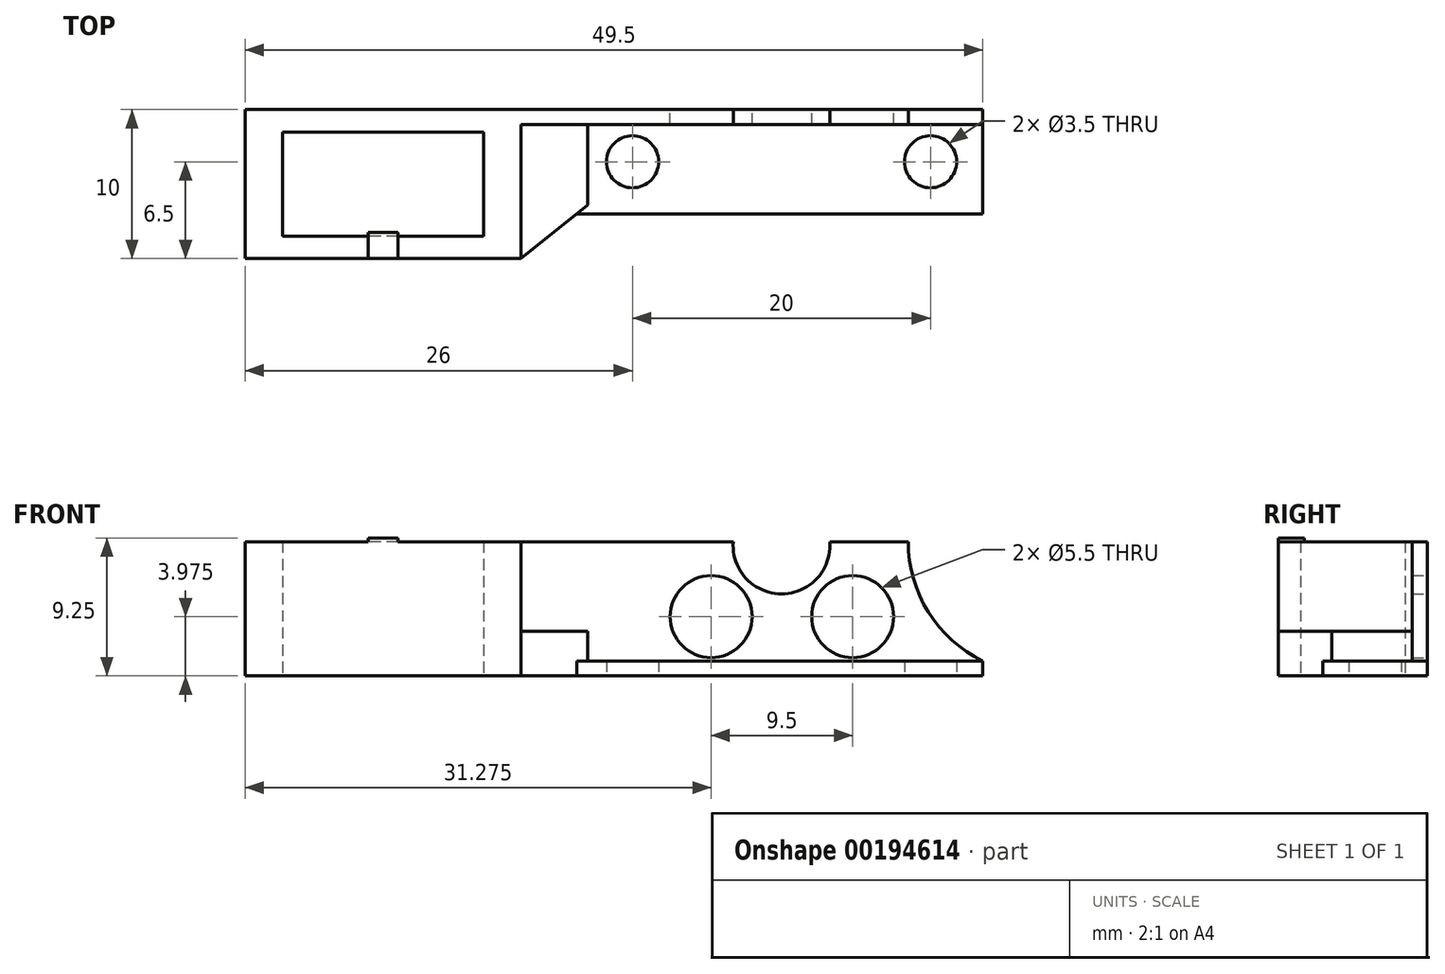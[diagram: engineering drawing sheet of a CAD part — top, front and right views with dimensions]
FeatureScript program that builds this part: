
annotation { "Feature Type Name" : "Feature", "Feature Type Description" : "" }
export const myFeature = defineFeature(function(context is Context, id is Id, definition is map)
    precondition{}
    {
        {
            var Q0;
            Q0=qCreatedBy(makeId("Top.planeOp"),FACE);
            var sketch = newSketch(context, id + "F0", { "sketchPlane" : qUnion([Q0])});
            skLineSegment(sketch, "E0.bottom", {"start": v(6.75, 3.5) * mm, "end": v(-6.75, 3.5) * mm});
            skLineSegment(sketch, "E0.top", {"start": v(6.75, -3.5) * mm, "end": v(-6.75, -3.5) * mm});
            skLineSegment(sketch, "E0.left", {"start": v(6.75, 3.5) * mm, "end": v(6.75, -3.5) * mm});
            skLineSegment(sketch, "E0.right", {"start": v(-6.75, 3.5) * mm, "end": v(-6.75, -3.5) * mm});
            skPoint(sketch, "E0.middle", {"position": v(0, 0) * mm});
            skLineSegment(sketch, "E1.bottom", {"start": v(-9.25, 5) * mm, "end": v(9.25, 5) * mm});
            skLineSegment(sketch, "E1.top", {"start": v(-9.25, -5) * mm, "end": v(9.25, -5) * mm});
            skLineSegment(sketch, "E1.left", {"start": v(-9.25, 5) * mm, "end": v(-9.25, -5) * mm});
            skLineSegment(sketch, "E1.right", {"start": v(9.25, 5) * mm, "end": v(9.25, -5) * mm});
            skSolve(sketch);
        }
        {
            var Q0;
            Q0=makeQuery(id+"F0.imprint","IMPRINT",FACE,{"disambiguationData":[TD([[makeQuery(id+"F0.imprint","IMPRINT",EDGE,{"derivedFrom":sQuery(id+"F0.wireOp",EDGE,"E0.bottom")}),-1.0]])]});
            extrude(context, id + "F1", {"entities" : qUnion([Q0]), "depth" : 9 * mm});
        }
        {
            var Q0;
            Q0=makeQuery(id+"F1.opExtrude","CAP_FACE",FACE,{"disambiguationData":[OSD([sQuery(id+"F0.wireOp",EDGE,"E0.bottom"),sQuery(id+"F0.wireOp",EDGE,"E0.top"),sQuery(id+"F0.wireOp",EDGE,"E0.left"),sQuery(id+"F0.wireOp",EDGE,"E0.right"),sQuery(id+"F0.wireOp",EDGE,"E1.bottom"),sQuery(id+"F0.wireOp",EDGE,"E1.top"),sQuery(id+"F0.wireOp",EDGE,"E1.left"),sQuery(id+"F0.wireOp",EDGE,"E1.right")])],"isStart":true});
            var sketch = newSketch(context, id + "F2", { "sketchPlane" : qUnion([Q0])});
            skLineSegment(sketch, "E2.bottom", {"start": v(14.25, -5) * mm, "end": v(39.25, -5) * mm});
            skLineSegment(sketch, "E2.top", {"start": v(14.25, 1) * mm, "end": v(39.25, 1) * mm});
            skLineSegment(sketch, "E2.left", {"start": v(14.25, -5) * mm, "end": v(14.25, 1) * mm});
            skLineSegment(sketch, "E2.right", {"start": v(39.25, -5) * mm, "end": v(39.25, 1) * mm});
            skLineSegment(sketch, "E3", {"start": v(14.25, -4) * mm, "end": v(39.25, -4) * mm});
            skLineSegment(sketch, "E4", {"start": v(19.25, 1) * mm, "end": v(19.25, -4) * mm, "construction": true});
            skLineSegment(sketch, "E5", {"start": v(34.25, 1) * mm, "end": v(34.25, -4) * mm, "construction": true});
            skLineSegment(sketch, "E6", {"start": v(34.25, -4) * mm, "end": v(39.25, 1) * mm, "construction": true});
            skLineSegment(sketch, "E7", {"start": v(14.25, 1) * mm, "end": v(19.25, -4) * mm, "construction": true});
            skLineSegment(sketch, "E8", {"start": v(14.25, -5) * mm, "end": v(9.25, -5) * mm});
            skLineSegment(sketch, "E9", {"start": v(9.25, -5) * mm, "end": v(9.25, 5) * mm});
            skLineSegment(sketch, "E10", {"start": v(9.25, 5) * mm, "end": v(14.25, 1) * mm});
            skCircle(sketch, "E11", {"center": v(16.75, -1.5) * mm, "radius": 1.75 * mm});
            skCircle(sketch, "E12", {"center": v(36.75, -1.5) * mm, "radius": 1.75 * mm});
            skLineSegment(sketch, "E13", {"start": v(39.25, -5) * mm, "end": v(40.25, -5) * mm});
            skLineSegment(sketch, "E14", {"start": v(40.25, -5) * mm, "end": v(40.25, 2) * mm});
            skLineSegment(sketch, "E15", {"start": v(40.25, 2) * mm, "end": v(13, 2) * mm});
            skLineSegment(sketch, "E16", {"start": v(13.75, -5) * mm, "end": v(13.75, 1.4) * mm});
            skSolve(sketch);
        }
        {
            var Q0;
            {var subQ3=sQuery(id+"F2.wireOp",EDGE,"E9");Q0=makeQuery(id+"F2.imprint","IMPRINT",FACE,{"disambiguationData":[TD([[makeQuery(id+"F2.imprint","IMPRINT",EDGE,{"derivedFrom":subQ3}),-1.0]])]});}
            extrude(context, id + "F3", {"entities" : qUnion([Q0]), "operationType" : NewBodyOperationType.ADD, "oppositeDirection" : true, "depth" : 3 * mm});
        }
        {
            var Q0;
            {var subQ3=sQuery(id+"F2.wireOp",EDGE,"E16");Q0=makeQuery(id+"F2.imprint","IMPRINT",FACE,{"disambiguationData":[TD([[makeQuery(id+"F2.imprint","IMPRINT",EDGE,{"derivedFrom":subQ3}),-1.0]])]});}
            var Q1;
            {var subQ1=sQuery(id+"F2.wireOp",EDGE,"E2.top");Q1=makeQuery(id+"F2.imprint","IMPRINT",FACE,{"disambiguationData":[TD([[makeQuery(id+"F2.imprint","IMPRINT",EDGE,{"derivedFrom":subQ1}),1.0]])]});}
            var Q2;
            {var subQ0=sQuery(id+"F2.wireOp",EDGE,"E2.bottom");Q2=makeQuery(id+"F2.imprint","IMPRINT",FACE,{"disambiguationData":[TD([[makeQuery(id+"F2.imprint","IMPRINT",EDGE,{"derivedFrom":subQ0}),1.0]])]});}
            var Q3;
            {var subQ2=sQuery(id+"F2.wireOp",EDGE,"E2.top");Q3=makeQuery(id+"F2.imprint","IMPRINT",FACE,{"disambiguationData":[TD([[makeQuery(id+"F2.imprint","IMPRINT",EDGE,{"derivedFrom":subQ2}),-1.0]])]});}
            extrude(context, id + "F4", {"entities" : qUnion([Q0, Q1, Q2, Q3]), "operationType" : NewBodyOperationType.ADD, "oppositeDirection" : true, "depth" : 1 * mm});
        }
        {
            var Q0;
            {var subQ0=sQuery(id+"F2.wireOp",EDGE,"E8");Q0=makeQuery(id+"F4.boolean.opBoolean","MERGE",FACE,{"derivedFrom":[makeQuery(id+"F3.boolean.opBoolean","MERGE",FACE,{"derivedFrom":[makeQuery(id+"F1.opExtrude","SWEPT_FACE",FACE,{"disambiguationData":[OSD([sQuery(id+"F0.wireOp",EDGE,"E1.bottom")])]}),makeQuery(id+"F3.opExtrude","SWEPT_FACE",FACE,{"disambiguationData":[OSD([subQ0])]})]}),makeQuery(id+"F4.opExtrude","SWEPT_FACE",FACE,{"disambiguationData":[OSD([sQuery(id+"F2.wireOp",EDGE,"E2.bottom"),subQ0,sQuery(id+"F2.wireOp",EDGE,"E13")])]})]});}
            var sketch = newSketch(context, id + "F5", { "sketchPlane" : qUnion([Q0])});
            skLineSegment(sketch, "E17.bottom", {"start": v(-14.25, 1) * mm, "end": v(-39.25, 1) * mm});
            skLineSegment(sketch, "E17.top", {"start": v(-14.25, 16.5) * mm, "end": v(-39.25, 16.5) * mm});
            skLineSegment(sketch, "E17.left", {"start": v(-14.25, 1) * mm, "end": v(-14.25, 16.5) * mm});
            skLineSegment(sketch, "E17.right", {"start": v(-39.25, 1) * mm, "end": v(-39.25, 16.5) * mm});
            skLineSegment(sketch, "E18", {"start": v(-26.75, 16.5) * mm, "end": v(-26.75, 1) * mm, "construction": true});
            skLineSegment(sketch, "E19", {"start": v(-39.25, 8.75) * mm, "end": v(-14.25, 8.75) * mm, "construction": true});
            skCircle(sketch, "E20", {"center": v(-26.75, 8.75) * mm, "radius": 3.25 * mm});
            skLineSegment(sketch, "E21", {"start": v(-22.02, 16.5) * mm, "end": v(-22.02, 1) * mm, "construction": true});
            skLineSegment(sketch, "E22", {"start": v(-31.52, 16.5) * mm, "end": v(-31.52, 1) * mm, "construction": true});
            skLineSegment(sketch, "E23", {"start": v(-31.52, 3.97) * mm, "end": v(-22.02, 3.98) * mm, "construction": true});
            skLineSegment(sketch, "E24", {"start": v(-31.52, 13.47) * mm, "end": v(-22.02, 13.48) * mm, "construction": true});
            skCircle(sketch, "E25", {"center": v(-22.02, 13.48) * mm, "radius": 2.75 * mm});
            skCircle(sketch, "E26", {"center": v(-22.02, 3.98) * mm, "radius": 2.75 * mm});
            skCircle(sketch, "E27", {"center": v(-31.52, 3.97) * mm, "radius": 2.75 * mm});
            skCircle(sketch, "E28", {"center": v(-31.52, 13.47) * mm, "radius": 2.75 * mm});
            skLineSegment(sketch, "E29.bottom", {"start": v(-14.25, 16.5) * mm, "end": v(-9.25, 16.5) * mm});
            skLineSegment(sketch, "E29.top", {"start": v(-14.25, 1) * mm, "end": v(-9.25, 1) * mm});
            skLineSegment(sketch, "E29.left", {"start": v(-14.25, 16.5) * mm, "end": v(-14.25, 1) * mm});
            skLineSegment(sketch, "E29.right", {"start": v(-9.25, 16.5) * mm, "end": v(-9.25, 1) * mm});
            skLineSegment(sketch, "E30.bottom", {"start": v(-39.25, 16.5) * mm, "end": v(-40.25, 16.5) * mm});
            skLineSegment(sketch, "E30.top", {"start": v(-39.25, 1) * mm, "end": v(-40.25, 1) * mm});
            skLineSegment(sketch, "E30.left", {"start": v(-39.25, 16.5) * mm, "end": v(-39.25, 1) * mm});
            skLineSegment(sketch, "E30.right", {"start": v(-40.25, 16.5) * mm, "end": v(-40.25, 1) * mm});
            skLineSegment(sketch, "E31", {"start": v(-9.25, 9) * mm, "end": v(-40.25, 9) * mm});
            skArc(sketch, "E32", {"start": v(-40.25, 1) * mm, "mid": v(-36.6, 4.28) * mm, "end": v(-35.25, 9) * mm});
            skSolve(sketch);
        }
        {
            var Q0;
            {var subQ1=sQuery(id+"F5.wireOp",EDGE,"E17.bottom");Q0=makeQuery(id+"F5.imprint","IMPRINT",FACE,{"disambiguationData":[TD([[makeQuery(id+"F5.imprint","IMPRINT",EDGE,{"derivedFrom":subQ1}),1.0]])]});}
            var Q1;
            {var subQ5=sQuery(id+"F2.wireOp",EDGE,"E8");var subQ6=makeQuery(id+"F3.opExtrude","CAP_EDGE",EDGE,{"disambiguationData":[OSD([subQ5])],"isStart":false});Q1=makeQuery(id+"F5.imprint","IMPRINT",FACE,{"disambiguationData":[TD([[makeQuery(id+"F5.imprint","IMPRINT",EDGE,{"derivedFrom":subQ6}),1.0]])]});}
            var Q2;
            {var subQ0=sQuery(id+"F5.wireOp",EDGE,"E30.top");Q2=makeQuery(id+"F5.imprint","IMPRINT",FACE,{"disambiguationData":[TD([[makeQuery(id+"F5.imprint","IMPRINT",EDGE,{"derivedFrom":subQ0}),1.0]])]});}
            extrude(context, id + "F6", {"entities" : qUnion([Q0, Q1, Q2]), "operationType" : NewBodyOperationType.ADD, "oppositeDirection" : true, "depth" : 1 * mm});
        }
        {
            var Q0;
            {var subQ0=sQuery(id+"F5.wireOp",EDGE,"E31");var subQ1=makeQuery(id+"F5.imprint","INTERSECT",VERTEX,{"derivedFrom":[sQuery(id+"F5.wireOp",EDGE,"E29.left"),subQ0]});var subQ2=sQuery(id+"F0.wireOp",EDGE,"E1.bottom");Q0=makeQuery(id+"F6.boolean.opBoolean","MERGE",FACE,{"derivedFrom":[makeQuery(id+"F1.opExtrude","CAP_FACE",FACE,{"disambiguationData":[OSD([sQuery(id+"F0.wireOp",EDGE,"E0.bottom"),sQuery(id+"F0.wireOp",EDGE,"E0.top"),sQuery(id+"F0.wireOp",EDGE,"E0.left"),sQuery(id+"F0.wireOp",EDGE,"E0.right"),subQ2,sQuery(id+"F0.wireOp",EDGE,"E1.top"),sQuery(id+"F0.wireOp",EDGE,"E1.left"),sQuery(id+"F0.wireOp",EDGE,"E1.right")])],"isStart":false}),makeQuery(id+"F6.opExtrude","SWEPT_FACE",FACE,{"disambiguationData":[OSD([subQ0]),TDD([makeQuery(id+"F5.imprint","IMPRINT",EDGE,{"disambiguationData":[TD([[subQ1,1.0]])],"derivedFrom":subQ0}),makeQuery(id+"F5.imprint","IMPRINT",EDGE,{"disambiguationData":[TD([[makeQuery(id+"F5.imprint","INTERSECT",VERTEX,{"disambiguationData":[OD(0.0)],"derivedFrom":[sQuery(id+"F5.wireOp",EDGE,"E20"),subQ0]}),1.0]])],"derivedFrom":subQ0})])]})]});}
            var sketch = newSketch(context, id + "F7", { "sketchPlane" : qUnion([Q0])});
            skLineSegment(sketch, "E33", {"start": v(0, -5) * mm, "end": v(0, -3.25) * mm, "construction": true});
            skPoint(sketch, "E33.endSnap0", {"position": v(0, -3.5) * mm});
            skLineSegment(sketch, "E34.bottom", {"start": v(1, -5) * mm, "end": v(-1, -5) * mm});
            skLineSegment(sketch, "E34.top", {"start": v(1, -3.25) * mm, "end": v(-1, -3.25) * mm});
            skLineSegment(sketch, "E34.left", {"start": v(1, -5) * mm, "end": v(1, -3.25) * mm});
            skLineSegment(sketch, "E34.right", {"start": v(-1, -5) * mm, "end": v(-1, -3.25) * mm});
            skSolve(sketch);
        }
        {
            var Q0;
            Q0 = qSketchRegion(id + "F7", true);
            extrude(context, id + "F8", {"entities" : qUnion([Q0]), "operationType" : NewBodyOperationType.ADD, "depth" : .25 * mm});
        }
    });
